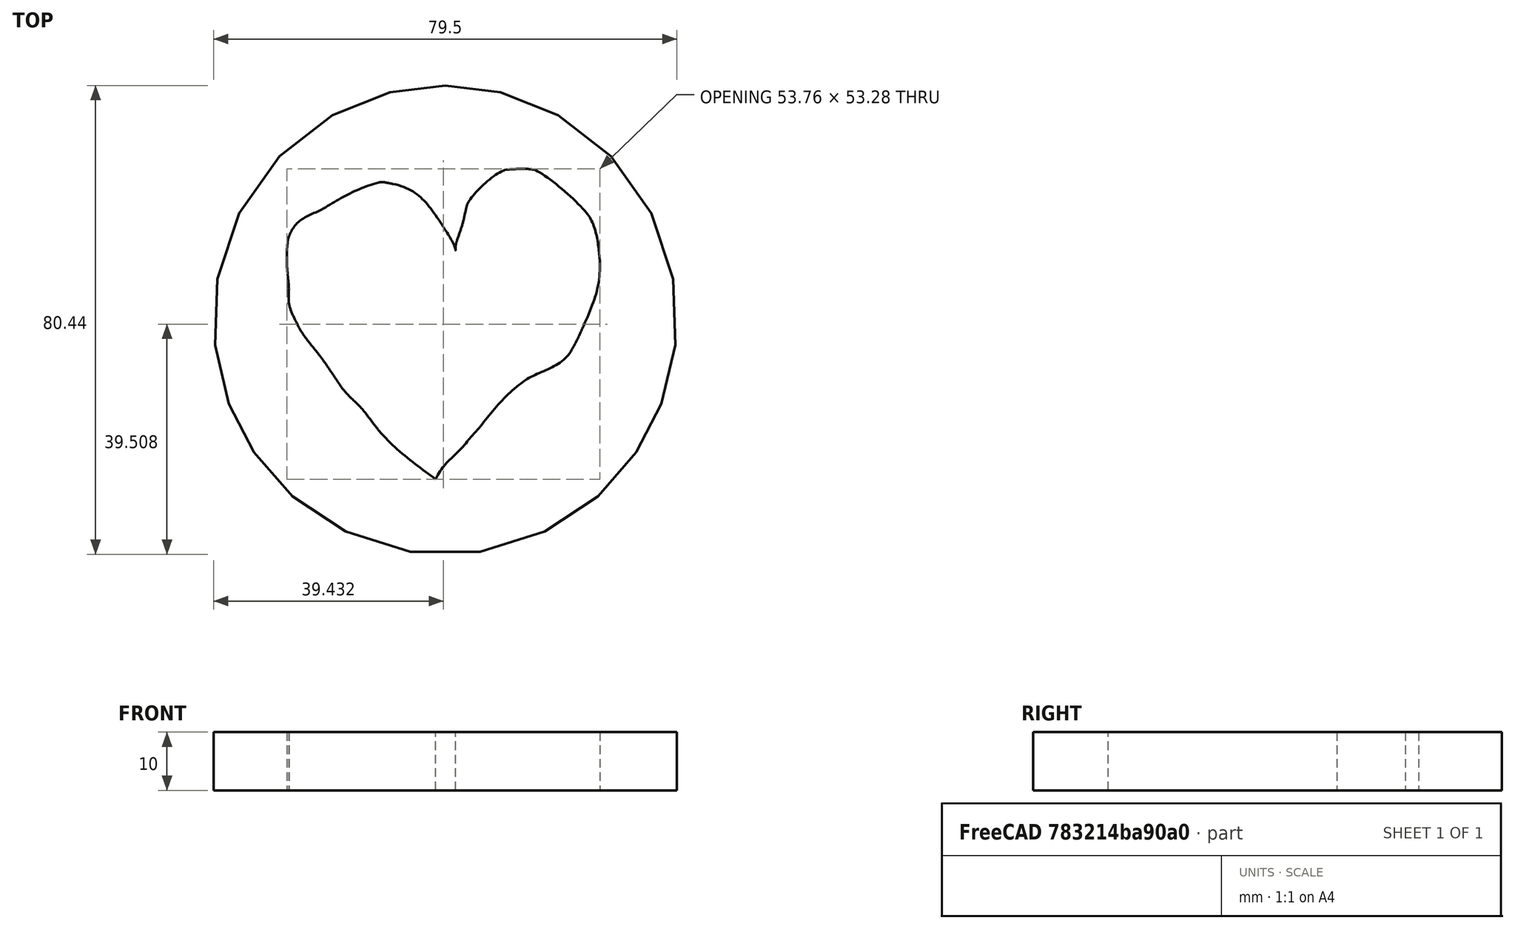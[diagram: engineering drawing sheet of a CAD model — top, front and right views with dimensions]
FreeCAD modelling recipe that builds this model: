
FCSTD DOCUMENT  (FreeCAD 0.20R29177 +233 (Git))
Label: Moneda-corazon-svg
License: Creative Commons Attribution-ShareAlike
LicenseURL: http://creativecommons.org/licenses/by-sa/4.0/
objects: Part::Feature×2, Part::Extrusion×2, Part::Cut×1
note: 5 computed .brp shape members not serialized (recipe doc carries the construction recipe); baked Part::Feature solids carry a one-line shape summary decoded from their .brp

FEATURE [Part::Feature] path111
  Placement = pos=(-11.4886,-247.815,0) rot=(0,0,1;1.5708rad)
  shape: bbox 96.16 x 88.8 x 2e-07 mm, 0 faces, 0 solids (baked)
FEATURE [Part::Feature] path176
  shape: bbox 54.04 x 53.39 x 2e-07 mm, 0 faces, 0 solids (baked)
FEATURE [Part::Extrusion] Extrude
  Base = -> path176
  Dir = (0,0,-1)
  DirMode = 2
  FaceMakerClass = Part::FaceMakerBullseye
  LengthFwd = -10
  LengthRev = 0
  Solid = true
  Symmetric = false
FEATURE [Part::Extrusion] Extrude001
  Base = -> path111
  Dir = (0,0,1)
  DirMode = 2
  FaceMakerClass = Part::FaceMakerBullseye
  LengthFwd = 10
  LengthRev = 0
  Solid = true
  Symmetric = false
FEATURE [Part::Cut] Cut
  Base = -> Extrude001
  Refine = true
  Tool = -> Extrude
